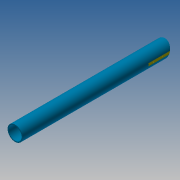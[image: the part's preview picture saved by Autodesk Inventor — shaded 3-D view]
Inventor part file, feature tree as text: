
AUTODESK INVENTOR PART (.ipt)
format: ipt  version: 2014 SP1 (Build 180222100, 222)  size: 123,904 bytes
history: native  units: in
note: dims shown in document units (in); Inventor stores cm internally (conversion verified against a paired STEP export)
features: sketch x6, extrude x3, plane x3, hole x1
ambient origin geometry x8: Origin, YZ Plane, XZ Plane, XY Plane, X Axis, Y Axis, Z Axis, Center Point
bodies: Solid1 (feature_tree)
feature tree (13):
  extrude  "tube"  Depth=0.1575in
  sketch  "Sketch15"  dims[d3=24.685in d4=0.0in d66=1.2205in]
  plane  "Work Plane6"
  plane  "Work Plane7"
  extrude  "flatFaceYellow"  Depth=1.2205in
  sketch  "Sketch21"  dims[d69=1.0in d70=0.0in d86=0.1361in]
  plane  "Work Plane8"
  extrude  "angledEnd"  Depth=3.937in
  hole  "Hole3"  [1 undecoded]
  sketch  "Sketch1"  dims[d0=2.4803in d2=0.1575in]
  sketch  "Sketch19"  dims[d67=0.7874in d68=3.937in]
  sketch  "Sketch22"  dims[d87=1.0in d88=0.0in]
  sketch  "Sketch23"  dims[d89=3.1496in d90=0.7874in d92=1.5748in d93=0.3937in d95=1.0in d97=0.0787in d98=0.75in d99=0.375in d100=0.25in d101=0.5635in d102=1.0in d103=0.8108in]
note: 1 required parameter value undecoded (feature->parameter linkage not recoverable at this tier; creation-order binding heuristic only, values carry confidence <= 0.55)
